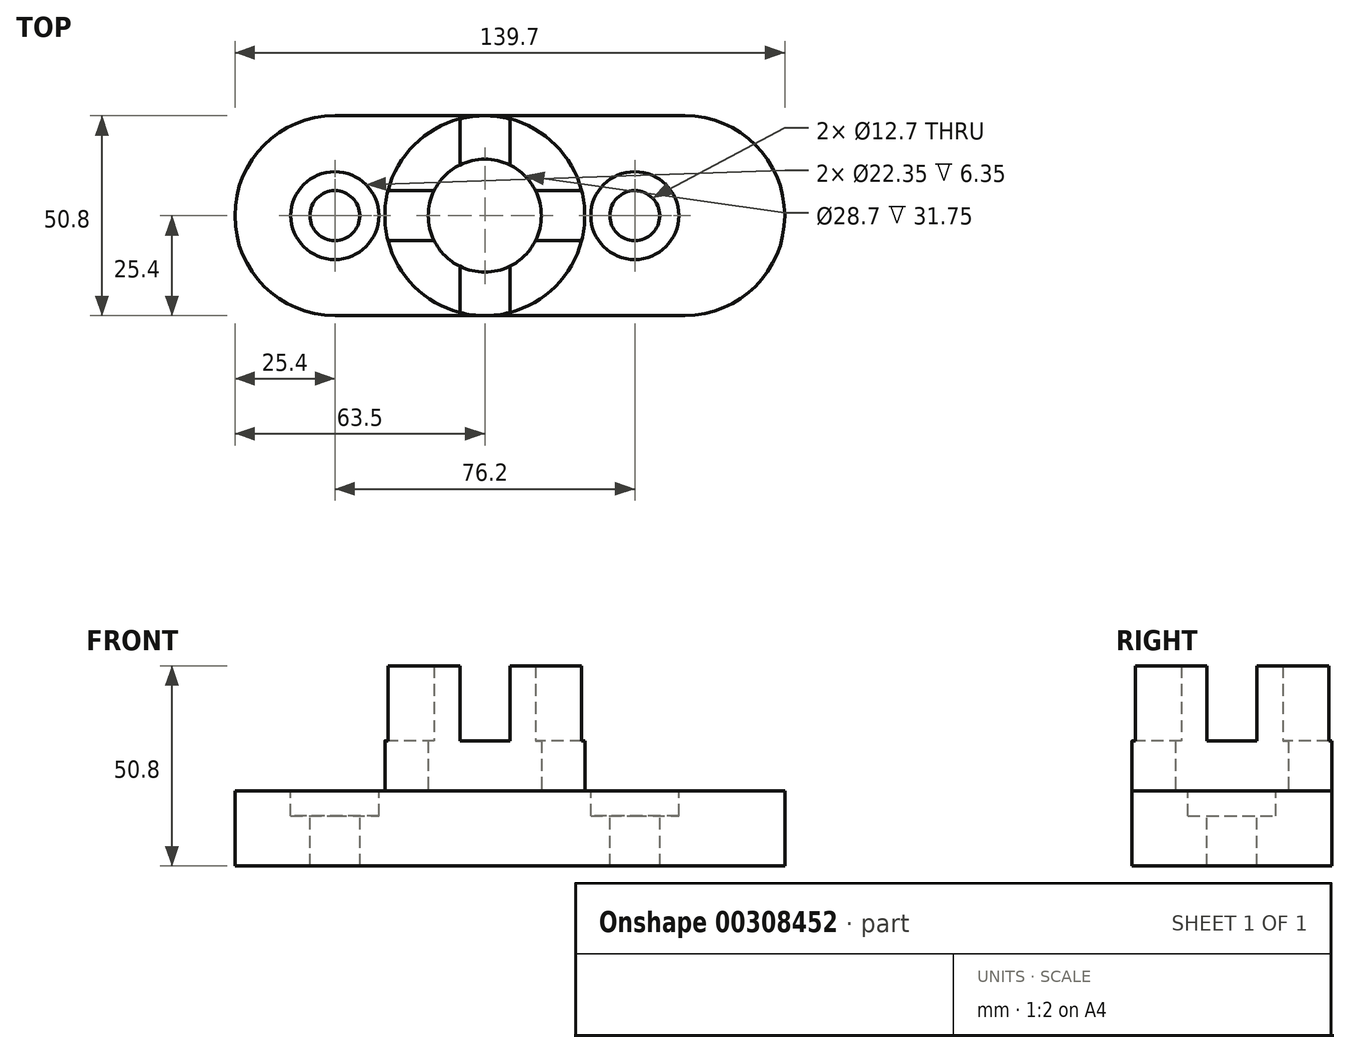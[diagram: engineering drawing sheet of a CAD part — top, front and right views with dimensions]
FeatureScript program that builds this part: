
annotation { "Feature Type Name" : "Feature", "Feature Type Description" : "" }
export const myFeature = defineFeature(function(context is Context, id is Id, definition is map)
    precondition{}
    {
        {
            var Q0;
            Q0=qCreatedBy(makeId("Front.planeOp"),FACE);
            var sketch = newSketch(context, id + "F0", { "sketchPlane" : qUnion([Q0])});
            skArc(sketch, "E0", {"start": v(0, 25.4) * mm, "mid": v(-25.4, 0) * mm, "end": v(0, -25.4) * mm});
            skLineSegment(sketch, "E1", {"start": v(0, 0) * mm, "end": v(44.45, 0) * mm, "construction": true});
            skLineSegment(sketch, "E2", {"start": v(44.45, 0) * mm, "end": v(88.9, 0) * mm, "construction": true});
            skArc(sketch, "E3", {"start": v(88.9, 25.4) * mm, "mid": v(114.3, 0) * mm, "end": v(88.9, -25.4) * mm});
            skLineSegment(sketch, "E4", {"start": v(0, 25.4) * mm, "end": v(88.9, 25.4) * mm});
            skLineSegment(sketch, "E5", {"start": v(88.9, -25.4) * mm, "end": v(0, -25.4) * mm});
            skSolve(sketch);
        }
        {
            var Q0;
            Q0=makeQuery(id+"F0.imprint","IMPRINT",FACE,{"disambiguationData":[TD([[makeQuery(id+"F0.imprint","IMPRINT",EDGE,{"derivedFrom":sQuery(id+"F0.wireOp",EDGE,"E0")}),1.0]])]});
            extrude(context, id + "F1", {"entities" : qUnion([Q0]), "depth" : 19.05 * mm});
        }
        {
            var Q0;
            Q0=makeQuery(id+"F1.opExtrude","SWEPT_BODY",BODY,{"disambiguationData":[OSD([sQuery(id+"F0.wireOp",EDGE,"E0"),sQuery(id+"F0.wireOp",EDGE,"E3"),sQuery(id+"F0.wireOp",EDGE,"E4"),sQuery(id+"F0.wireOp",EDGE,"E5")])]});
            var Q1;
            Q1=makeQuery(id+"F1.opExtrude","CAP_EDGE",EDGE,{"disambiguationData":[OSD([sQuery(id+"F0.wireOp",EDGE,"E5")])],"isStart":false});
            transform(context, id + "F2", {"entities" : qUnion([Q0]), "transformType" : TransformType.ROTATION, "transformAxis" : qUnion([Q1]), "angle" : 90 * degree, "makeCopy" : false});
        }
        {
            var Q0;
            Q0=makeQuery(id+"F1.opExtrude","CAP_FACE",FACE,{"disambiguationData":[OSD([sQuery(id+"F0.wireOp",EDGE,"E0"),sQuery(id+"F0.wireOp",EDGE,"E3"),sQuery(id+"F0.wireOp",EDGE,"E4"),sQuery(id+"F0.wireOp",EDGE,"E5")])],"isStart":false});
            var sketch = newSketch(context, id + "F3", { "sketchPlane" : qUnion([Q0])});
            skLineSegment(sketch, "E6", {"start": v(0, 31.75) * mm, "end": v(0, 6.35) * mm, "construction": true});
            skLineSegment(sketch, "E7", {"start": v(0, 6.35) * mm, "end": v(76.2, 6.35) * mm, "construction": true});
            skLineSegment(sketch, "E8", {"start": v(76.2, 6.35) * mm, "end": v(76.2, 31.75) * mm, "construction": true});
            skCircle(sketch, "E9", {"center": v(0, 6.35) * mm, "radius": 6.35 * mm});
            skCircle(sketch, "E10", {"center": v(76.2, 6.35) * mm, "radius": 6.35 * mm});
            skLineSegment(sketch, "E11", {"start": v(0, 6.35) * mm, "end": v(38.1, 6.35) * mm, "construction": true});
            skCircle(sketch, "E12", {"center": v(38.1, 6.35) * mm, "radius": 25.4 * mm});
            skCircle(sketch, "E13", {"center": v(38.1, 6.35) * mm, "radius": 14.35 * mm});
            skCircle(sketch, "E14", {"center": v(0, 6.35) * mm, "radius": 11.18 * mm});
            skCircle(sketch, "E15", {"center": v(76.2, 6.35) * mm, "radius": 11.18 * mm});
            skSolve(sketch);
        }
        {
            var Q0;
            Q0=makeQuery(id+"F3.imprint","IMPRINT",FACE,{"disambiguationData":[TD([[makeQuery(id+"F3.imprint","IMPRINT",EDGE,{"derivedFrom":sQuery(id+"F3.wireOp",EDGE,"E10")}),1.0]])]});
            var Q1;
            Q1=makeQuery(id+"F3.imprint","IMPRINT",FACE,{"disambiguationData":[TD([[makeQuery(id+"F3.imprint","IMPRINT",EDGE,{"derivedFrom":sQuery(id+"F3.wireOp",EDGE,"E9")}),1.0]])]});
            var Q2;
            Q2=sQuery(id+"F3.wireOp",EDGE,"E10");
            var Q3;
            Q3=sQuery(id+"F3.wireOp",EDGE,"E9");
            extrude(context, id + "F4", {"entities" : qUnion([Q0, Q1]), "operationType" : NewBodyOperationType.REMOVE, "surfaceEntities" : qUnion([Q2, Q3]), "oppositeDirection" : true, "depth" : 25.4 * mm});
        }
        {
            var Q0;
            Q0=makeQuery(id+"F3.imprint","IMPRINT",FACE,{"disambiguationData":[TD([[makeQuery(id+"F3.imprint","IMPRINT",EDGE,{"derivedFrom":sQuery(id+"F3.wireOp",EDGE,"E13")}),-1.0]])]});
            var Q1;
            Q1=sQuery(id+"F3.wireOp",EDGE,"E13");
            var Q2;
            Q2=sQuery(id+"F3.wireOp",EDGE,"E12");
            extrude(context, id + "F5", {"entities" : qUnion([Q0]), "operationType" : NewBodyOperationType.ADD, "surfaceEntities" : qUnion([Q1, Q2]), "depth" : 31.75 * mm});
        }
        {
            var Q0;
            Q0=makeQuery(id+"F5.opExtrude","CAP_FACE",FACE,{"disambiguationData":[OSD([sQuery(id+"F3.wireOp",EDGE,"E12"),sQuery(id+"F3.wireOp",EDGE,"E13")])],"isStart":false});
            var sketch = newSketch(context, id + "F6", { "sketchPlane" : qUnion([Q0])});
            skLineSegment(sketch, "E16.bottom", {"start": v(44.45, 46.6) * mm, "end": v(31.75, 46.6) * mm});
            skLineSegment(sketch, "E16.top", {"start": v(44.45, -33.9) * mm, "end": v(31.75, -33.9) * mm});
            skLineSegment(sketch, "E16.left", {"start": v(44.45, 46.6) * mm, "end": v(44.45, -33.9) * mm});
            skLineSegment(sketch, "E16.right", {"start": v(31.75, 46.6) * mm, "end": v(31.75, -33.9) * mm});
            skPoint(sketch, "E16.middle", {"position": v(38.1, 6.35) * mm});
            skLineSegment(sketch, "E17.bottom", {"start": v(80.15, 0) * mm, "end": v(-3.95, 0) * mm});
            skLineSegment(sketch, "E17.top", {"start": v(80.15, 12.7) * mm, "end": v(-3.95, 12.7) * mm});
            skLineSegment(sketch, "E17.left", {"start": v(80.15, 0) * mm, "end": v(80.15, 12.7) * mm});
            skLineSegment(sketch, "E17.right", {"start": v(-3.95, 0) * mm, "end": v(-3.95, 12.7) * mm});
            skSolve(sketch);
        }
        {
            var Q0;
            Q0 = qSketchRegion(id + "F6", true);
            extrude(context, id + "F7", {"entities" : qUnion([Q0]), "operationType" : NewBodyOperationType.REMOVE, "oppositeDirection" : true, "depth" : 19.05 * mm});
        }
        {
            var Q0;
            Q0=makeQuery(id+"F3.imprint","IMPRINT",FACE,{"disambiguationData":[TD([[makeQuery(id+"F3.imprint","IMPRINT",EDGE,{"derivedFrom":sQuery(id+"F3.wireOp",EDGE,"E10")}),-1.0]])]});
            var Q1;
            Q1=makeQuery(id+"F3.imprint","IMPRINT",FACE,{"disambiguationData":[TD([[makeQuery(id+"F3.imprint","IMPRINT",EDGE,{"derivedFrom":sQuery(id+"F3.wireOp",EDGE,"E9")}),-1.0]])]});
            var Q2;
            Q2=sQuery(id+"F3.wireOp",EDGE,"E15");
            var Q3;
            Q3=sQuery(id+"F3.wireOp",EDGE,"E14");
            var Q4;
            Q4=sQuery(id+"F3.wireOp",EDGE,"E9");
            var Q5;
            Q5=sQuery(id+"F3.wireOp",EDGE,"E10");
            extrude(context, id + "F8", {"entities" : qUnion([Q0, Q1]), "operationType" : NewBodyOperationType.REMOVE, "surfaceEntities" : qUnion([Q2, Q3, Q4, Q5]), "oppositeDirection" : true, "depth" : 6.35 * mm});
        }
    });
